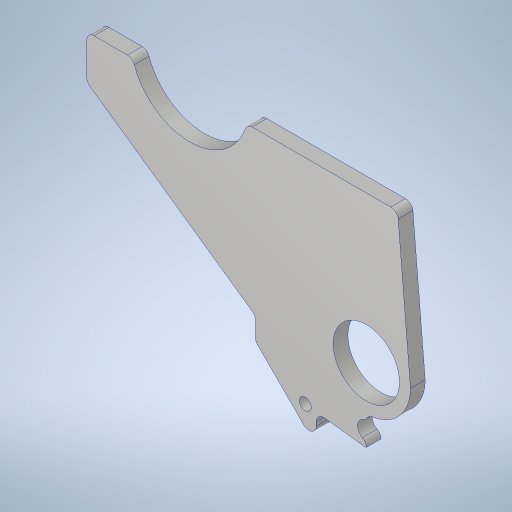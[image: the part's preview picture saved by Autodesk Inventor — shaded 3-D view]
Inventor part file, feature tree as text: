
AUTODESK INVENTOR PART (.ipt)
format: ipt  version: 2023.4 (Build 274418000, 418)  size: 315,904 bytes
history: native  units: in
note: dims shown in document units (in); Inventor stores cm internally (conversion verified against a paired STEP export)
features: fillet x3, sketch x1, extrude x1, chamfer x1, hole x1
ambient origin geometry x8: Origin, YZ Plane, XZ Plane, XY Plane, X Axis, Y Axis, Z Axis, Center Point
bodies: Solid1 (feature_tree)
feature tree (7):
  sketch  "Sketch1"  dims[d0=4.0in d1=5.5in d3=2.0in d4=0.25in d6=0.75in d7=1.5in d8=1.5in d9=1.125in d10=0.8589in d11=1.25in d12=3.5in d15=0.35in d18=0.6528in d19=0.25in d20=0.0in d21=0.125in d25=0.3in d26=1.0in d28=0.1875in d31=0.25in d33=0.85in d34=0.875in d35=0.125in d36=45.0deg d37=0.125in d38=3.0in d39=0.125in d40=0.375in d42=0.201in d43=0.75in d44=0.385in d45=0.25in d46=0.5635in d47=1.0in d48=0.8108in d49=0.375in]
  extrude  "Extrusion1"  Depth=1.0in
  fillet  "Fillet1"  Radius=2.0in
  chamfer  "Chamfer1"  Distance=0.25in
  fillet  "Fillet3"  Radius=0.75in
  fillet  "Fillet4"  Radius=1.5in
  hole  "Hole1"  [1 undecoded]
note: 1 required parameter value undecoded (feature->parameter linkage not recoverable at this tier; creation-order binding heuristic only, values carry confidence <= 0.55)
